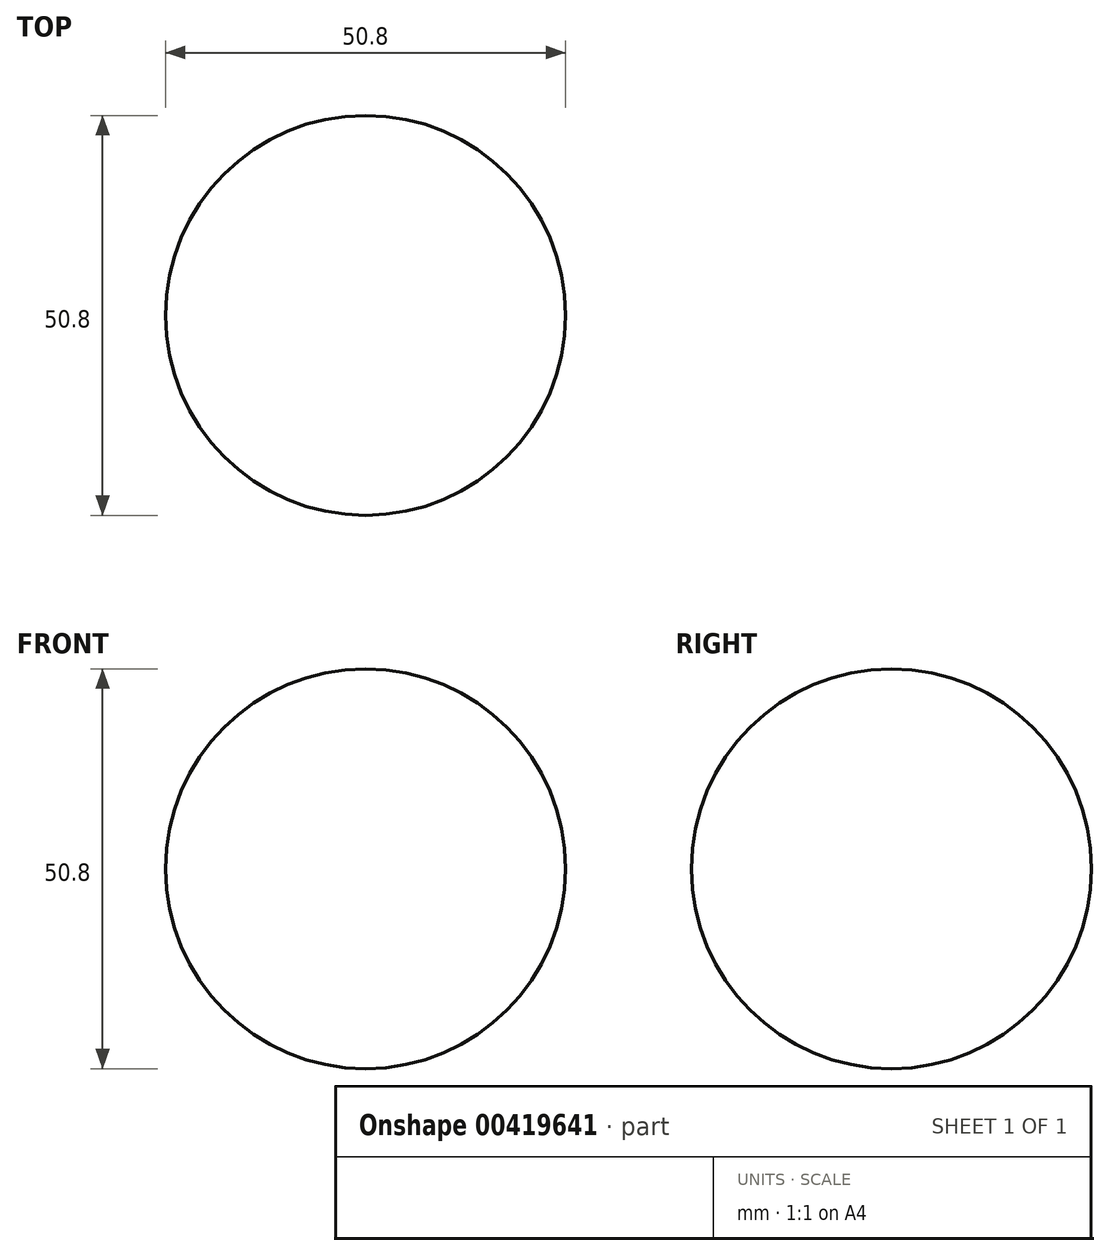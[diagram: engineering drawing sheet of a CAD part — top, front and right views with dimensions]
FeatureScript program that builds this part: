
annotation { "Feature Type Name" : "Feature", "Feature Type Description" : "" }
export const myFeature = defineFeature(function(context is Context, id is Id, definition is map)
    precondition{}
    {
        {
            var Q0;
            Q0=qCreatedBy(makeId("Front.planeOp"),FACE);
            var sketch = newSketch(context, id + "F0", { "sketchPlane" : qUnion([Q0])});
            skArc(sketch, "E0", {"start": v(0, 25.4) * mm, "mid": v(-25.4, 0) * mm, "end": v(0, -25.4) * mm});
            skLineSegment(sketch, "E1", {"start": v(0, 25.4) * mm, "end": v(0, -25.4) * mm});
            skSolve(sketch);
        }
        {
            var Q0;
            Q0=sQuery(id+"F0.wireOp",EDGE,"E0");
            var Q1;
            Q1=sQuery(id+"F0.wireOp",EDGE,"E1");
            revolve(context, id + "F1", {"bodyType" : ToolBodyType.SURFACE, "surfaceEntities" : qUnion([Q0]), "axis" : qUnion([Q1]), "revolveType" : RevolveType.FULL});
        }
    });
